# Revit family: Storage-Freestanding-Teknion-BFRL_Full_Solid_Door_Tower-R2018
name_source: partatom
category: Furniture
revit_build: Autodesk Revit 2018 (Build: 20170223_1515(x64)
units: mm (PartAtom-declared; Revit-internal decimal feet)

## family parameters
Always vertical = Yes
Cut with Voids When Loaded = No
OmniClass Number = 23.40.70.14.64.21
OmniClass Title = Systems Furniture
Room Calculation Point = No
Shared = Yes
Work Plane-Based = No

## types (2) — shared parameters
Assembly Code = E2020200
Manufacturer = Teknion
Manufacturer Fax = 416.661.4586
Part Number = BFRL
Product Documentation Link = http://www.teknion.com
Product Line = Expansion Casegoods
Product Page URL = http://www.teknion.com
Series = Expansion Casegoods
Sustainability Data = http://www.teknion.com
URL = http://www.teknion.com
Unit Weight URL = http://www.teknion.com
Warranty = http://www.teknion.com

## per-type parameters (varying)
| type | Actual Height | Description | Height | Model |
| 18"w x 66"h | 65.165 " | Freestanding Tower with Full Solid Door, 18"w, 66"h | 66 " | BFRL___1866_ |
| 18"w x 72"h | 71.406 " | Freestanding Tower with Full Solid Door, 18"w, 72"h | 72 " | BFRL___1872_ |

## geometry (parser evidence)
native form markers: Blend x132, Sweep x3
no freeform markers — native parametric forms only
